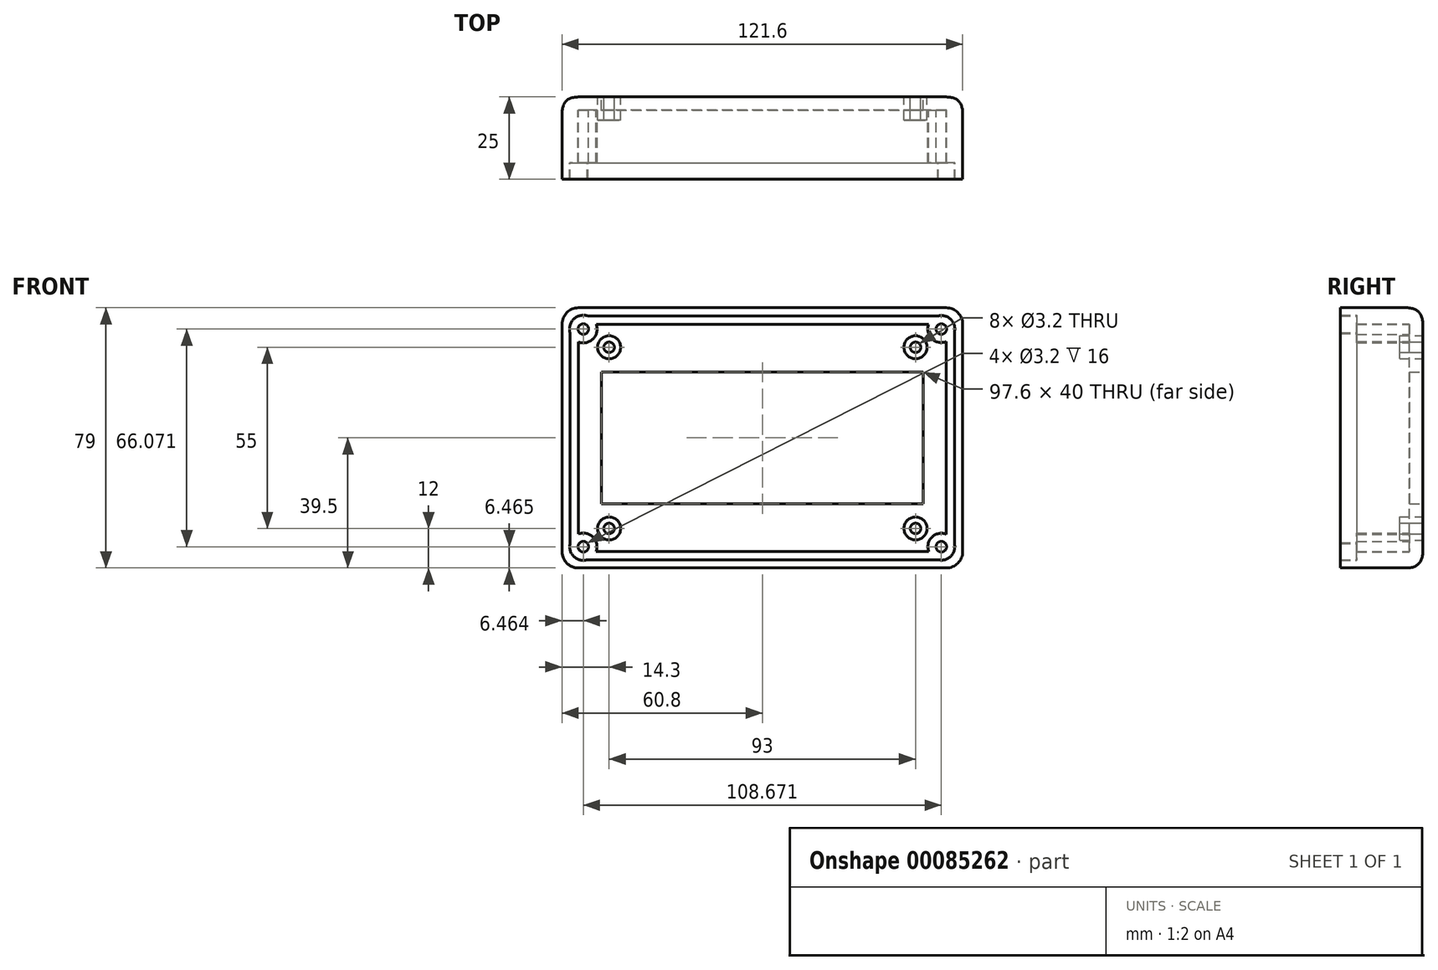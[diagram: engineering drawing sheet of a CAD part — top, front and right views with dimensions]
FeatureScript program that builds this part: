
annotation { "Feature Type Name" : "Feature", "Feature Type Description" : "" }
export const myFeature = defineFeature(function(context is Context, id is Id, definition is map)
    precondition{}
    {
        {
            var Q0;
            Q0=qCreatedBy(makeId("Front.planeOp"),FACE);
            var sketch = newSketch(context, id + "F0", { "sketchPlane" : qUnion([Q0])});
            skLineSegment(sketch, "E0.bottom", {"start": v(55.8, 39.5) * mm, "end": v(-55.8, 39.5) * mm});
            skLineSegment(sketch, "E0.top", {"start": v(55.8, -39.5) * mm, "end": v(-55.8, -39.5) * mm});
            skLineSegment(sketch, "E0.left", {"start": v(60.8, 34.5) * mm, "end": v(60.8, -34.5) * mm});
            skLineSegment(sketch, "E0.right", {"start": v(-60.8, 34.5) * mm, "end": v(-60.8, -34.5) * mm});
            skPoint(sketch, "E0.middle", {"position": v(0, 0) * mm});
            skPoint(sketch, "E1.visualSharp", {"position": v(-60.8, 39.5) * mm});
            skArc(sketch, "E1.filletArc", {"start": v(-55.8, 39.5) * mm, "mid": v(-59.34, 38.04) * mm, "end": v(-60.8, 34.5) * mm});
            skPoint(sketch, "E2.visualSharp", {"position": v(60.8, 39.5) * mm});
            skArc(sketch, "E2.filletArc", {"start": v(60.8, 34.5) * mm, "mid": v(59.34, 38.04) * mm, "end": v(55.8, 39.5) * mm});
            skPoint(sketch, "E3.visualSharp", {"position": v(60.8, -39.5) * mm});
            skArc(sketch, "E3.filletArc", {"start": v(55.8, -39.5) * mm, "mid": v(59.34, -38.04) * mm, "end": v(60.8, -34.5) * mm});
            skPoint(sketch, "E4.visualSharp", {"position": v(-60.8, -39.5) * mm});
            skArc(sketch, "E4.filletArc", {"start": v(-60.8, -34.5) * mm, "mid": v(-59.34, -38.04) * mm, "end": v(-55.8, -39.5) * mm});
            skLineSegment(sketch, "E5.bottom", {"start": v(-46.5, 27.5) * mm, "end": v(46.5, 27.5) * mm});
            skLineSegment(sketch, "E5.top", {"start": v(-46.5, -27.5) * mm, "end": v(46.5, -27.5) * mm});
            skLineSegment(sketch, "E5.left", {"start": v(-46.5, 27.5) * mm, "end": v(-46.5, -27.5) * mm});
            skLineSegment(sketch, "E5.right", {"start": v(46.5, 27.5) * mm, "end": v(46.5, -27.5) * mm});
            skCircle(sketch, "E6", {"center": v(-46.5, 27.5) * mm, "radius": 1.6 * mm});
            skCircle(sketch, "E7", {"center": v(-46.5, 27.5) * mm, "radius": 3.5 * mm});
            skCircle(sketch, "E8", {"center": v(46.5, 27.5) * mm, "radius": 1.6 * mm});
            skCircle(sketch, "E9", {"center": v(46.5, 27.5) * mm, "radius": 3.5 * mm});
            skCircle(sketch, "E10", {"center": v(46.5, -27.5) * mm, "radius": 1.6 * mm});
            skCircle(sketch, "E11", {"center": v(46.5, -27.5) * mm, "radius": 3.5 * mm});
            skCircle(sketch, "E12", {"center": v(-46.5, -27.5) * mm, "radius": 1.6 * mm});
            skCircle(sketch, "E13", {"center": v(-46.5, -27.5) * mm, "radius": 3.5 * mm});
            skLineSegment(sketch, "E14.bottom", {"start": v(-48.8, 20) * mm, "end": v(48.8, 20) * mm});
            skLineSegment(sketch, "E14.top", {"start": v(-48.8, -20) * mm, "end": v(48.8, -20) * mm});
            skLineSegment(sketch, "E14.left", {"start": v(-48.8, 20) * mm, "end": v(-48.8, -20) * mm});
            skLineSegment(sketch, "E14.right", {"start": v(48.8, 20) * mm, "end": v(48.8, -20) * mm});
            skLineSegment(sketch, "E15.bottom", {"start": v(-50.8, 34.5) * mm, "end": v(50.8, 34.5) * mm});
            skLineSegment(sketch, "E15.top", {"start": v(-50.8, -34.5) * mm, "end": v(50.8, -34.5) * mm});
            skLineSegment(sketch, "E15.left", {"start": v(-55.8, 29.5) * mm, "end": v(-55.8, -29.5) * mm});
            skLineSegment(sketch, "E15.right", {"start": v(55.8, 29.5) * mm, "end": v(55.8, -29.5) * mm});
            skArc(sketch, "E16.filletArc", {"start": v(-50.8, 34.5) * mm, "mid": v(-54.34, 33.04) * mm, "end": v(-55.8, 29.5) * mm});
            skArc(sketch, "E17.filletArc", {"start": v(55.8, 29.5) * mm, "mid": v(54.34, 33.04) * mm, "end": v(50.8, 34.5) * mm});
            skArc(sketch, "E18.filletArc", {"start": v(50.8, -34.5) * mm, "mid": v(54.34, -33.04) * mm, "end": v(55.8, -29.5) * mm});
            skArc(sketch, "E19.filletArc", {"start": v(-55.8, -29.5) * mm, "mid": v(-54.34, -33.04) * mm, "end": v(-50.8, -34.5) * mm});
            skLineSegment(sketch, "E20.bottom", {"start": v(-53.3, 37) * mm, "end": v(53.3, 37) * mm});
            skLineSegment(sketch, "E20.top", {"start": v(-53.3, -37) * mm, "end": v(53.3, -37) * mm});
            skLineSegment(sketch, "E20.left", {"start": v(-58.3, 32) * mm, "end": v(-58.3, -32) * mm});
            skLineSegment(sketch, "E20.right", {"start": v(58.3, 32) * mm, "end": v(58.3, -32) * mm});
            skPoint(sketch, "E21.visualSharp", {"position": v(-58.3, 37) * mm});
            skArc(sketch, "E21.filletArc", {"start": v(-53.3, 37) * mm, "mid": v(-56.84, 35.54) * mm, "end": v(-58.3, 32) * mm});
            skPoint(sketch, "E22.visualSharp", {"position": v(58.3, 37) * mm});
            skArc(sketch, "E22.filletArc", {"start": v(58.3, 32) * mm, "mid": v(56.84, 35.54) * mm, "end": v(53.3, 37) * mm});
            skPoint(sketch, "E23.visualSharp", {"position": v(58.3, -37) * mm});
            skArc(sketch, "E23.filletArc", {"start": v(53.3, -37) * mm, "mid": v(56.84, -35.54) * mm, "end": v(58.3, -32) * mm});
            skPoint(sketch, "E24.visualSharp", {"position": v(-58.3, -37) * mm});
            skArc(sketch, "E24.filletArc", {"start": v(-58.3, -32) * mm, "mid": v(-56.84, -35.54) * mm, "end": v(-53.3, -37) * mm});
            skCircle(sketch, "E25", {"center": v(-54.34, 33.04) * mm, "radius": 4.2 * mm});
            skCircle(sketch, "E26", {"center": v(-54.34, 33.04) * mm, "radius": 1.6 * mm});
            skCircle(sketch, "E27", {"center": v(54.34, 33.04) * mm, "radius": 1.6 * mm});
            skCircle(sketch, "E28", {"center": v(54.34, 33.04) * mm, "radius": 4.1 * mm});
            skCircle(sketch, "E29", {"center": v(54.34, -33.04) * mm, "radius": 1.6 * mm});
            skCircle(sketch, "E30", {"center": v(54.34, -33.04) * mm, "radius": 4.09 * mm});
            skCircle(sketch, "E31", {"center": v(-54.34, -33.04) * mm, "radius": 1.6 * mm});
            skCircle(sketch, "E32", {"center": v(-54.34, -33.04) * mm, "radius": 4.14 * mm});
            skSolve(sketch);
        }
        {
            var Q0;
            {var subQ0=sQuery(id+"F0.wireOp",EDGE,"E6");var subQ1=sQuery(id+"F0.wireOp",EDGE,"E5.bottom");var subQ2=makeQuery(id+"F0.imprint","INTERSECT",VERTEX,{"derivedFrom":[subQ1,subQ0]});Q0=makeQuery(id+"F0.imprint","IMPRINT",FACE,{"disambiguationData":[TD([[makeQuery(id+"F0.imprint","IMPRINT",EDGE,{"disambiguationData":[TD([[subQ2,-1.0]])],"derivedFrom":subQ1}),1.0]])]});}
            var Q1;
            {var subQ0=sQuery(id+"F0.wireOp",EDGE,"E6");var subQ1=sQuery(id+"F0.wireOp",EDGE,"E5.bottom");var subQ2=makeQuery(id+"F0.imprint","INTERSECT",VERTEX,{"derivedFrom":[subQ1,subQ0]});Q1=makeQuery(id+"F0.imprint","IMPRINT",FACE,{"disambiguationData":[TD([[makeQuery(id+"F0.imprint","IMPRINT",EDGE,{"disambiguationData":[TD([[subQ2,-1.0]])],"derivedFrom":subQ1}),-1.0]])]});}
            var Q2;
            {var subQ3=sQuery(id+"F0.wireOp",EDGE,"E12");var subQ9=sQuery(id+"F0.wireOp",EDGE,"E5.top");var subQ12=makeQuery(id+"F0.imprint","INTERSECT",VERTEX,{"derivedFrom":[subQ9,subQ3]});Q2=makeQuery(id+"F0.imprint","IMPRINT",FACE,{"disambiguationData":[TD([[makeQuery(id+"F0.imprint","IMPRINT",EDGE,{"disambiguationData":[TD([[subQ12,-1.0]])],"derivedFrom":subQ9}),1.0]])]});}
            var Q3;
            {var subQ0=sQuery(id+"F0.wireOp",EDGE,"E12");var subQ1=sQuery(id+"F0.wireOp",EDGE,"E5.top");var subQ2=makeQuery(id+"F0.imprint","INTERSECT",VERTEX,{"derivedFrom":[subQ1,subQ0]});Q3=makeQuery(id+"F0.imprint","IMPRINT",FACE,{"disambiguationData":[TD([[makeQuery(id+"F0.imprint","IMPRINT",EDGE,{"disambiguationData":[TD([[subQ2,-1.0]])],"derivedFrom":subQ1}),-1.0]])]});}
            var Q4;
            {var subQ0=sQuery(id+"F0.wireOp",EDGE,"E11");var subQ1=sQuery(id+"F0.wireOp",EDGE,"E5.top");var subQ2=makeQuery(id+"F0.imprint","INTERSECT",VERTEX,{"derivedFrom":[subQ1,subQ0]});Q4=makeQuery(id+"F0.imprint","IMPRINT",FACE,{"disambiguationData":[TD([[makeQuery(id+"F0.imprint","IMPRINT",EDGE,{"disambiguationData":[TD([[subQ2,-1.0]])],"derivedFrom":subQ1}),-1.0]])]});}
            var Q5;
            {var subQ1=sQuery(id+"F0.wireOp",EDGE,"E5.top");var subQ5=sQuery(id+"F0.wireOp",EDGE,"E11");var subQ6=makeQuery(id+"F0.imprint","INTERSECT",VERTEX,{"derivedFrom":[subQ1,subQ5]});Q5=makeQuery(id+"F0.imprint","IMPRINT",FACE,{"disambiguationData":[TD([[makeQuery(id+"F0.imprint","IMPRINT",EDGE,{"disambiguationData":[TD([[subQ6,-1.0]])],"derivedFrom":subQ1}),1.0]])]});}
            var Q6;
            {var subQ0=sQuery(id+"F0.wireOp",EDGE,"E13");var subQ1=sQuery(id+"F0.wireOp",EDGE,"E5.top");var subQ2=makeQuery(id+"F0.imprint","INTERSECT",VERTEX,{"derivedFrom":[subQ1,subQ0]});Q6=makeQuery(id+"F0.imprint","IMPRINT",FACE,{"disambiguationData":[TD([[makeQuery(id+"F0.imprint","IMPRINT",EDGE,{"disambiguationData":[TD([[subQ2,-1.0]])],"derivedFrom":subQ1}),1.0]])]});}
            var Q7;
            {var subQ0=sQuery(id+"F0.wireOp",EDGE,"E9");var subQ1=sQuery(id+"F0.wireOp",EDGE,"E5.bottom");var subQ2=makeQuery(id+"F0.imprint","INTERSECT",VERTEX,{"derivedFrom":[subQ1,subQ0]});Q7=makeQuery(id+"F0.imprint","IMPRINT",FACE,{"disambiguationData":[TD([[makeQuery(id+"F0.imprint","IMPRINT",EDGE,{"disambiguationData":[TD([[subQ2,-1.0]])],"derivedFrom":subQ1}),1.0]])]});}
            var Q8;
            {var subQ0=sQuery(id+"F0.wireOp",EDGE,"E9");var subQ1=sQuery(id+"F0.wireOp",EDGE,"E5.bottom");var subQ2=makeQuery(id+"F0.imprint","INTERSECT",VERTEX,{"derivedFrom":[subQ1,subQ0]});Q8=makeQuery(id+"F0.imprint","IMPRINT",FACE,{"disambiguationData":[TD([[makeQuery(id+"F0.imprint","IMPRINT",EDGE,{"disambiguationData":[TD([[subQ2,-1.0]])],"derivedFrom":subQ1}),-1.0]])]});}
            var Q9;
            {var subQ5=sQuery(id+"F0.wireOp",EDGE,"E7");var subQ9=sQuery(id+"F0.wireOp",EDGE,"E5.bottom");var subQ10=makeQuery(id+"F0.imprint","INTERSECT",VERTEX,{"derivedFrom":[subQ9,subQ5]});Q9=makeQuery(id+"F0.imprint","IMPRINT",FACE,{"disambiguationData":[TD([[makeQuery(id+"F0.imprint","IMPRINT",EDGE,{"disambiguationData":[TD([[subQ10,-1.0]])],"derivedFrom":subQ9}),-1.0]])]});}
            var Q10;
            {var subQ12=sQuery(id+"F0.wireOp",EDGE,"E14.left");Q10=makeQuery(id+"F0.imprint","IMPRINT",FACE,{"disambiguationData":[TD([[makeQuery(id+"F0.imprint","IMPRINT",EDGE,{"derivedFrom":subQ12}),-1.0]])]});}
            var Q11;
            {var subQ4=sQuery(id+"F0.wireOp",EDGE,"E15.bottom");Q11=makeQuery(id+"F0.imprint","IMPRINT",FACE,{"disambiguationData":[TD([[makeQuery(id+"F0.imprint","IMPRINT",EDGE,{"derivedFrom":subQ4}),1.0]])]});}
            var Q12;
            Q12=makeQuery(id+"F0.imprint","IMPRINT",FACE,{"disambiguationData":[TD([[makeQuery(id+"F0.imprint","IMPRINT",EDGE,{"derivedFrom":sQuery(id+"F0.wireOp",EDGE,"E15.top")}),-1.0]])]});
            var Q13;
            {var subQ0=sQuery(id+"F0.wireOp",EDGE,"E16.filletArc");var subQ5=sQuery(id+"F0.wireOp",EDGE,"E15.bottom");var subQ6=makeQuery(id+"F0.imprint","INTERSECT",VERTEX,{"derivedFrom":[subQ5,subQ0]});Q13=makeQuery(id+"F0.imprint","IMPRINT",FACE,{"disambiguationData":[TD([[makeQuery(id+"F0.imprint","IMPRINT",EDGE,{"disambiguationData":[TD([[subQ6,-1.0]])],"derivedFrom":subQ5}),-1.0]])]});}
            var Q14;
            {var subQ0=sQuery(id+"F0.wireOp",EDGE,"E21.filletArc");Q14=makeQuery(id+"F0.imprint","IMPRINT",FACE,{"disambiguationData":[TD([[makeQuery(id+"F0.imprint","IMPRINT",EDGE,{"derivedFrom":subQ0}),-1.0]])]});}
            var Q15;
            {var subQ0=sQuery(id+"F0.wireOp",EDGE,"E24.filletArc");Q15=makeQuery(id+"F0.imprint","IMPRINT",FACE,{"disambiguationData":[TD([[makeQuery(id+"F0.imprint","IMPRINT",EDGE,{"derivedFrom":subQ0}),-1.0]])]});}
            var Q16;
            {var subQ11=sQuery(id+"F0.wireOp",EDGE,"E24.filletArc");Q16=makeQuery(id+"F0.imprint","IMPRINT",FACE,{"disambiguationData":[TD([[makeQuery(id+"F0.imprint","IMPRINT",EDGE,{"derivedFrom":subQ11}),1.0]])]});}
            var Q17;
            {var subQ0=sQuery(id+"F0.wireOp",EDGE,"E19.filletArc");var subQ1=sQuery(id+"F0.wireOp",EDGE,"E15.top");var subQ2=makeQuery(id+"F0.imprint","INTERSECT",VERTEX,{"derivedFrom":[subQ1,subQ0]});Q17=makeQuery(id+"F0.imprint","IMPRINT",FACE,{"disambiguationData":[TD([[makeQuery(id+"F0.imprint","IMPRINT",EDGE,{"disambiguationData":[TD([[subQ2,-1.0]])],"derivedFrom":subQ1}),1.0]])]});}
            var Q18;
            {var subQ0=sQuery(id+"F0.wireOp",EDGE,"E25");var subQ1=sQuery(id+"F0.wireOp",EDGE,"E15.left");var subQ2=makeQuery(id+"F0.imprint","INTERSECT",VERTEX,{"derivedFrom":[subQ1,subQ0]});Q18=makeQuery(id+"F0.imprint","IMPRINT",FACE,{"disambiguationData":[TD([[makeQuery(id+"F0.imprint","IMPRINT",EDGE,{"disambiguationData":[TD([[subQ2,-1.0]])],"derivedFrom":subQ1}),-1.0]])]});}
            var Q19;
            {var subQ11=sQuery(id+"F0.wireOp",EDGE,"E21.filletArc");Q19=makeQuery(id+"F0.imprint","IMPRINT",FACE,{"disambiguationData":[TD([[makeQuery(id+"F0.imprint","IMPRINT",EDGE,{"derivedFrom":subQ11}),1.0]])]});}
            var Q20;
            {var subQ0=sQuery(id+"F0.wireOp",EDGE,"E18.filletArc");var subQ1=sQuery(id+"F0.wireOp",EDGE,"E15.top");var subQ2=makeQuery(id+"F0.imprint","INTERSECT",VERTEX,{"derivedFrom":[subQ1,subQ0]});Q20=makeQuery(id+"F0.imprint","IMPRINT",FACE,{"disambiguationData":[TD([[makeQuery(id+"F0.imprint","IMPRINT",EDGE,{"disambiguationData":[TD([[subQ2,1.0]])],"derivedFrom":subQ1}),1.0]])]});}
            var Q21;
            {var subQ0=sQuery(id+"F0.wireOp",EDGE,"E18.filletArc");var subQ1=sQuery(id+"F0.wireOp",EDGE,"E15.top");var subQ2=makeQuery(id+"F0.imprint","INTERSECT",VERTEX,{"derivedFrom":[subQ1,subQ0]});Q21=makeQuery(id+"F0.imprint","IMPRINT",FACE,{"disambiguationData":[TD([[makeQuery(id+"F0.imprint","IMPRINT",EDGE,{"disambiguationData":[TD([[subQ2,1.0]])],"derivedFrom":subQ1}),-1.0]])]});}
            var Q22;
            Q22=makeQuery(id+"F0.imprint","IMPRINT",FACE,{"disambiguationData":[TD([[makeQuery(id+"F0.imprint","IMPRINT",EDGE,{"derivedFrom":sQuery(id+"F0.wireOp",EDGE,"E0.bottom")}),1.0]])]});
            var Q23;
            {var subQ0=sQuery(id+"F0.wireOp",EDGE,"E30");var subQ1=sQuery(id+"F0.wireOp",EDGE,"E23.filletArc");var subQ2=makeQuery(id+"F0.imprint","INTERSECT",VERTEX,{"disambiguationData":[OD(0.0)],"derivedFrom":[subQ1,subQ0]});Q23=makeQuery(id+"F0.imprint","IMPRINT",FACE,{"disambiguationData":[TD([[makeQuery(id+"F0.imprint","IMPRINT",EDGE,{"disambiguationData":[TD([[subQ2,-1.0]])],"derivedFrom":subQ1}),-1.0]])]});}
            var Q24;
            {var subQ0=sQuery(id+"F0.wireOp",EDGE,"E28");var subQ1=sQuery(id+"F0.wireOp",EDGE,"E15.right");var subQ2=makeQuery(id+"F0.imprint","INTERSECT",VERTEX,{"derivedFrom":[subQ1,subQ0]});Q24=makeQuery(id+"F0.imprint","IMPRINT",FACE,{"disambiguationData":[TD([[makeQuery(id+"F0.imprint","IMPRINT",EDGE,{"disambiguationData":[TD([[subQ2,-1.0]])],"derivedFrom":subQ1}),1.0]])]});}
            var Q25;
            {var subQ0=sQuery(id+"F0.wireOp",EDGE,"E22.filletArc");Q25=makeQuery(id+"F0.imprint","IMPRINT",FACE,{"disambiguationData":[TD([[makeQuery(id+"F0.imprint","IMPRINT",EDGE,{"derivedFrom":subQ0}),-1.0]])]});}
            var Q26;
            {var subQ10=sQuery(id+"F0.wireOp",EDGE,"E22.filletArc");Q26=makeQuery(id+"F0.imprint","IMPRINT",FACE,{"disambiguationData":[TD([[makeQuery(id+"F0.imprint","IMPRINT",EDGE,{"derivedFrom":subQ10}),1.0]])]});}
            var Q27;
            {var subQ0=sQuery(id+"F0.wireOp",EDGE,"E17.filletArc");var subQ7=sQuery(id+"F0.wireOp",EDGE,"E15.bottom");var subQ8=makeQuery(id+"F0.imprint","INTERSECT",VERTEX,{"derivedFrom":[subQ7,subQ0]});Q27=makeQuery(id+"F0.imprint","IMPRINT",FACE,{"disambiguationData":[TD([[makeQuery(id+"F0.imprint","IMPRINT",EDGE,{"disambiguationData":[TD([[subQ8,1.0]])],"derivedFrom":subQ7}),-1.0]])]});}
            var Q28;
            {var subQ0=sQuery(id+"F0.wireOp",EDGE,"E26");var subQ1=sQuery(id+"F0.wireOp",EDGE,"E16.filletArc");var subQ2=makeQuery(id+"F0.imprint","INTERSECT",VERTEX,{"disambiguationData":[OD(0.0)],"derivedFrom":[subQ1,subQ0]});Q28=makeQuery(id+"F0.imprint","IMPRINT",FACE,{"disambiguationData":[TD([[makeQuery(id+"F0.imprint","IMPRINT",EDGE,{"disambiguationData":[TD([[subQ2,-1.0]])],"derivedFrom":subQ1}),-1.0]])]});}
            var Q29;
            {var subQ0=sQuery(id+"F0.wireOp",EDGE,"E26");var subQ1=sQuery(id+"F0.wireOp",EDGE,"E16.filletArc");var subQ2=makeQuery(id+"F0.imprint","INTERSECT",VERTEX,{"disambiguationData":[OD(0.0)],"derivedFrom":[subQ1,subQ0]});Q29=makeQuery(id+"F0.imprint","IMPRINT",FACE,{"disambiguationData":[TD([[makeQuery(id+"F0.imprint","IMPRINT",EDGE,{"disambiguationData":[TD([[subQ2,-1.0]])],"derivedFrom":subQ1}),1.0]])]});}
            var Q30;
            {var subQ0=sQuery(id+"F0.wireOp",EDGE,"E27");var subQ1=sQuery(id+"F0.wireOp",EDGE,"E17.filletArc");var subQ2=makeQuery(id+"F0.imprint","INTERSECT",VERTEX,{"disambiguationData":[OD(0.0)],"derivedFrom":[subQ1,subQ0]});Q30=makeQuery(id+"F0.imprint","IMPRINT",FACE,{"disambiguationData":[TD([[makeQuery(id+"F0.imprint","IMPRINT",EDGE,{"disambiguationData":[TD([[subQ2,-1.0]])],"derivedFrom":subQ1}),-1.0]])]});}
            var Q31;
            {var subQ0=sQuery(id+"F0.wireOp",EDGE,"E27");var subQ1=sQuery(id+"F0.wireOp",EDGE,"E17.filletArc");var subQ2=makeQuery(id+"F0.imprint","INTERSECT",VERTEX,{"disambiguationData":[OD(0.0)],"derivedFrom":[subQ1,subQ0]});Q31=makeQuery(id+"F0.imprint","IMPRINT",FACE,{"disambiguationData":[TD([[makeQuery(id+"F0.imprint","IMPRINT",EDGE,{"disambiguationData":[TD([[subQ2,-1.0]])],"derivedFrom":subQ1}),1.0]])]});}
            var Q32;
            {var subQ0=sQuery(id+"F0.wireOp",EDGE,"E29");var subQ1=sQuery(id+"F0.wireOp",EDGE,"E18.filletArc");var subQ2=makeQuery(id+"F0.imprint","INTERSECT",VERTEX,{"disambiguationData":[OD(0.0)],"derivedFrom":[subQ1,subQ0]});Q32=makeQuery(id+"F0.imprint","IMPRINT",FACE,{"disambiguationData":[TD([[makeQuery(id+"F0.imprint","IMPRINT",EDGE,{"disambiguationData":[TD([[subQ2,-1.0]])],"derivedFrom":subQ1}),-1.0]])]});}
            var Q33;
            {var subQ0=sQuery(id+"F0.wireOp",EDGE,"E29");var subQ1=sQuery(id+"F0.wireOp",EDGE,"E18.filletArc");var subQ2=makeQuery(id+"F0.imprint","INTERSECT",VERTEX,{"disambiguationData":[OD(0.0)],"derivedFrom":[subQ1,subQ0]});Q33=makeQuery(id+"F0.imprint","IMPRINT",FACE,{"disambiguationData":[TD([[makeQuery(id+"F0.imprint","IMPRINT",EDGE,{"disambiguationData":[TD([[subQ2,-1.0]])],"derivedFrom":subQ1}),1.0]])]});}
            var Q34;
            {var subQ0=sQuery(id+"F0.wireOp",EDGE,"E31");var subQ1=sQuery(id+"F0.wireOp",EDGE,"E19.filletArc");var subQ2=makeQuery(id+"F0.imprint","INTERSECT",VERTEX,{"disambiguationData":[OD(0.0)],"derivedFrom":[subQ1,subQ0]});Q34=makeQuery(id+"F0.imprint","IMPRINT",FACE,{"disambiguationData":[TD([[makeQuery(id+"F0.imprint","IMPRINT",EDGE,{"disambiguationData":[TD([[subQ2,-1.0]])],"derivedFrom":subQ1}),1.0]])]});}
            var Q35;
            {var subQ0=sQuery(id+"F0.wireOp",EDGE,"E31");var subQ1=sQuery(id+"F0.wireOp",EDGE,"E19.filletArc");var subQ2=makeQuery(id+"F0.imprint","INTERSECT",VERTEX,{"disambiguationData":[OD(0.0)],"derivedFrom":[subQ1,subQ0]});Q35=makeQuery(id+"F0.imprint","IMPRINT",FACE,{"disambiguationData":[TD([[makeQuery(id+"F0.imprint","IMPRINT",EDGE,{"disambiguationData":[TD([[subQ2,-1.0]])],"derivedFrom":subQ1}),-1.0]])]});}
            extrude(context, id + "F1", {"entities" : qUnion([Q0, Q1, Q2, Q3, Q4, Q5, Q6, Q7, Q8, Q9, Q10, Q11, Q12, Q13, Q14, Q15, Q16, Q17, Q18, Q19, Q20, Q21, Q22, Q23, Q24, Q25, Q26, Q27, Q28, Q29, Q30, Q31, Q32, Q33, Q34, Q35]), "depth" : 4 * mm});
        }
        {
            var Q0;
            {var subQ0=sQuery(id+"F0.wireOp",EDGE,"E12");var subQ1=sQuery(id+"F0.wireOp",EDGE,"E5.top");var subQ2=makeQuery(id+"F0.imprint","INTERSECT",VERTEX,{"derivedFrom":[subQ1,subQ0]});Q0=makeQuery(id+"F0.imprint","IMPRINT",FACE,{"disambiguationData":[TD([[makeQuery(id+"F0.imprint","IMPRINT",EDGE,{"disambiguationData":[TD([[subQ2,-1.0]])],"derivedFrom":subQ1}),-1.0]])]});}
            var Q1;
            {var subQ3=sQuery(id+"F0.wireOp",EDGE,"E12");var subQ9=sQuery(id+"F0.wireOp",EDGE,"E5.top");var subQ12=makeQuery(id+"F0.imprint","INTERSECT",VERTEX,{"derivedFrom":[subQ9,subQ3]});Q1=makeQuery(id+"F0.imprint","IMPRINT",FACE,{"disambiguationData":[TD([[makeQuery(id+"F0.imprint","IMPRINT",EDGE,{"disambiguationData":[TD([[subQ12,-1.0]])],"derivedFrom":subQ9}),1.0]])]});}
            var Q2;
            {var subQ0=sQuery(id+"F0.wireOp",EDGE,"E11");var subQ1=sQuery(id+"F0.wireOp",EDGE,"E5.top");var subQ2=makeQuery(id+"F0.imprint","INTERSECT",VERTEX,{"derivedFrom":[subQ1,subQ0]});Q2=makeQuery(id+"F0.imprint","IMPRINT",FACE,{"disambiguationData":[TD([[makeQuery(id+"F0.imprint","IMPRINT",EDGE,{"disambiguationData":[TD([[subQ2,-1.0]])],"derivedFrom":subQ1}),-1.0]])]});}
            var Q3;
            {var subQ1=sQuery(id+"F0.wireOp",EDGE,"E5.top");var subQ5=sQuery(id+"F0.wireOp",EDGE,"E11");var subQ6=makeQuery(id+"F0.imprint","INTERSECT",VERTEX,{"derivedFrom":[subQ1,subQ5]});Q3=makeQuery(id+"F0.imprint","IMPRINT",FACE,{"disambiguationData":[TD([[makeQuery(id+"F0.imprint","IMPRINT",EDGE,{"disambiguationData":[TD([[subQ6,-1.0]])],"derivedFrom":subQ1}),1.0]])]});}
            var Q4;
            {var subQ0=sQuery(id+"F0.wireOp",EDGE,"E9");var subQ1=sQuery(id+"F0.wireOp",EDGE,"E5.bottom");var subQ2=makeQuery(id+"F0.imprint","INTERSECT",VERTEX,{"derivedFrom":[subQ1,subQ0]});Q4=makeQuery(id+"F0.imprint","IMPRINT",FACE,{"disambiguationData":[TD([[makeQuery(id+"F0.imprint","IMPRINT",EDGE,{"disambiguationData":[TD([[subQ2,-1.0]])],"derivedFrom":subQ1}),1.0]])]});}
            var Q5;
            {var subQ0=sQuery(id+"F0.wireOp",EDGE,"E9");var subQ1=sQuery(id+"F0.wireOp",EDGE,"E5.bottom");var subQ2=makeQuery(id+"F0.imprint","INTERSECT",VERTEX,{"derivedFrom":[subQ1,subQ0]});Q5=makeQuery(id+"F0.imprint","IMPRINT",FACE,{"disambiguationData":[TD([[makeQuery(id+"F0.imprint","IMPRINT",EDGE,{"disambiguationData":[TD([[subQ2,-1.0]])],"derivedFrom":subQ1}),-1.0]])]});}
            var Q6;
            {var subQ0=sQuery(id+"F0.wireOp",EDGE,"E6");var subQ1=sQuery(id+"F0.wireOp",EDGE,"E5.bottom");var subQ2=makeQuery(id+"F0.imprint","INTERSECT",VERTEX,{"derivedFrom":[subQ1,subQ0]});Q6=makeQuery(id+"F0.imprint","IMPRINT",FACE,{"disambiguationData":[TD([[makeQuery(id+"F0.imprint","IMPRINT",EDGE,{"disambiguationData":[TD([[subQ2,-1.0]])],"derivedFrom":subQ1}),1.0]])]});}
            var Q7;
            {var subQ0=sQuery(id+"F0.wireOp",EDGE,"E6");var subQ1=sQuery(id+"F0.wireOp",EDGE,"E5.bottom");var subQ2=makeQuery(id+"F0.imprint","INTERSECT",VERTEX,{"derivedFrom":[subQ1,subQ0]});Q7=makeQuery(id+"F0.imprint","IMPRINT",FACE,{"disambiguationData":[TD([[makeQuery(id+"F0.imprint","IMPRINT",EDGE,{"disambiguationData":[TD([[subQ2,-1.0]])],"derivedFrom":subQ1}),-1.0]])]});}
            extrude(context, id + "F2", {"entities" : qUnion([Q0, Q1, Q2, Q3, Q4, Q5, Q6, Q7]), "depth" : 7 * mm});
        }
        {
            var Q0;
            Q0=makeQuery(id+"F0.imprint","IMPRINT",FACE,{"disambiguationData":[TD([[makeQuery(id+"F0.imprint","IMPRINT",EDGE,{"derivedFrom":sQuery(id+"F0.wireOp",EDGE,"E0.bottom")}),1.0]])]});
            extrude(context, id + "F3", {"entities" : qUnion([Q0]), "operationType" : NewBodyOperationType.ADD, "depth" : 25 * mm});
        }
        {
            var Q0;
            Q0=makeQuery(id+"F1.opExtrude","CAP_EDGE",EDGE,{"disambiguationData":[OSD([sQuery(id+"F0.wireOp",EDGE,"E2.filletArc")])],"isStart":true});
            var Q1;
            Q1=makeQuery(id+"F1.opExtrude","CAP_EDGE",EDGE,{"disambiguationData":[OSD([sQuery(id+"F0.wireOp",EDGE,"E0.left")])],"isStart":true});
            var Q2;
            Q2=makeQuery(id+"F1.opExtrude","CAP_EDGE",EDGE,{"disambiguationData":[OSD([sQuery(id+"F0.wireOp",EDGE,"E3.filletArc")])],"isStart":true});
            var Q3;
            Q3=makeQuery(id+"F1.opExtrude","CAP_EDGE",EDGE,{"disambiguationData":[OSD([sQuery(id+"F0.wireOp",EDGE,"E0.top")])],"isStart":true});
            var Q4;
            Q4=makeQuery(id+"F1.opExtrude","CAP_EDGE",EDGE,{"disambiguationData":[OSD([sQuery(id+"F0.wireOp",EDGE,"E4.filletArc")])],"isStart":true});
            var Q5;
            Q5=makeQuery(id+"F1.opExtrude","CAP_EDGE",EDGE,{"disambiguationData":[OSD([sQuery(id+"F0.wireOp",EDGE,"E0.right")])],"isStart":true});
            var Q6;
            Q6=makeQuery(id+"F1.opExtrude","CAP_EDGE",EDGE,{"disambiguationData":[OSD([sQuery(id+"F0.wireOp",EDGE,"E1.filletArc")])],"isStart":true});
            var Q7;
            Q7=makeQuery(id+"F1.opExtrude","CAP_EDGE",EDGE,{"disambiguationData":[OSD([sQuery(id+"F0.wireOp",EDGE,"E0.bottom")])],"isStart":true});
            fillet(context, id + "F4", {"entities" : qUnion([Q0, Q1, Q2, Q3, Q4, Q5, Q6, Q7]), "radius" : 5 * mm, "tangentPropagation" : true, "rho" : 0.5, "crossSection" : FilletCrossSection.CONIC, "allowEdgeOverflow" : false});
        }
        {
            var Q0;
            {var subQ0=sQuery(id+"F0.wireOp",EDGE,"E25");var subQ1=sQuery(id+"F0.wireOp",EDGE,"E15.bottom");var subQ2=makeQuery(id+"F0.imprint","INTERSECT",VERTEX,{"derivedFrom":[subQ1,subQ0]});Q0=makeQuery(id+"F0.imprint","IMPRINT",FACE,{"disambiguationData":[TD([[makeQuery(id+"F0.imprint","IMPRINT",EDGE,{"disambiguationData":[TD([[subQ2,-1.0]])],"derivedFrom":subQ1}),1.0]])]});}
            var Q1;
            {var subQ11=sQuery(id+"F0.wireOp",EDGE,"E21.filletArc");Q1=makeQuery(id+"F0.imprint","IMPRINT",FACE,{"disambiguationData":[TD([[makeQuery(id+"F0.imprint","IMPRINT",EDGE,{"derivedFrom":subQ11}),1.0]])]});}
            var Q2;
            {var subQ0=sQuery(id+"F0.wireOp",EDGE,"E16.filletArc");var subQ5=sQuery(id+"F0.wireOp",EDGE,"E15.bottom");var subQ6=makeQuery(id+"F0.imprint","INTERSECT",VERTEX,{"derivedFrom":[subQ5,subQ0]});Q2=makeQuery(id+"F0.imprint","IMPRINT",FACE,{"disambiguationData":[TD([[makeQuery(id+"F0.imprint","IMPRINT",EDGE,{"disambiguationData":[TD([[subQ6,-1.0]])],"derivedFrom":subQ5}),-1.0]])]});}
            var Q3;
            {var subQ0=sQuery(id+"F0.wireOp",EDGE,"E25");var subQ1=sQuery(id+"F0.wireOp",EDGE,"E15.left");var subQ2=makeQuery(id+"F0.imprint","INTERSECT",VERTEX,{"derivedFrom":[subQ1,subQ0]});Q3=makeQuery(id+"F0.imprint","IMPRINT",FACE,{"disambiguationData":[TD([[makeQuery(id+"F0.imprint","IMPRINT",EDGE,{"disambiguationData":[TD([[subQ2,-1.0]])],"derivedFrom":subQ1}),-1.0]])]});}
            var Q4;
            Q4=makeQuery(id+"F0.imprint","IMPRINT",FACE,{"disambiguationData":[TD([[makeQuery(id+"F0.imprint","IMPRINT",EDGE,{"derivedFrom":sQuery(id+"F0.wireOp",EDGE,"E0.bottom")}),1.0]])]});
            var Q5;
            {var subQ11=sQuery(id+"F0.wireOp",EDGE,"E24.filletArc");Q5=makeQuery(id+"F0.imprint","IMPRINT",FACE,{"disambiguationData":[TD([[makeQuery(id+"F0.imprint","IMPRINT",EDGE,{"derivedFrom":subQ11}),1.0]])]});}
            var Q6;
            {var subQ0=sQuery(id+"F0.wireOp",EDGE,"E19.filletArc");var subQ1=sQuery(id+"F0.wireOp",EDGE,"E15.top");var subQ2=makeQuery(id+"F0.imprint","INTERSECT",VERTEX,{"derivedFrom":[subQ1,subQ0]});Q6=makeQuery(id+"F0.imprint","IMPRINT",FACE,{"disambiguationData":[TD([[makeQuery(id+"F0.imprint","IMPRINT",EDGE,{"disambiguationData":[TD([[subQ2,-1.0]])],"derivedFrom":subQ1}),1.0]])]});}
            var Q7;
            {var subQ0=sQuery(id+"F0.wireOp",EDGE,"E18.filletArc");var subQ1=sQuery(id+"F0.wireOp",EDGE,"E15.top");var subQ2=makeQuery(id+"F0.imprint","INTERSECT",VERTEX,{"derivedFrom":[subQ1,subQ0]});Q7=makeQuery(id+"F0.imprint","IMPRINT",FACE,{"disambiguationData":[TD([[makeQuery(id+"F0.imprint","IMPRINT",EDGE,{"disambiguationData":[TD([[subQ2,1.0]])],"derivedFrom":subQ1}),-1.0]])]});}
            var Q8;
            {var subQ0=sQuery(id+"F0.wireOp",EDGE,"E18.filletArc");var subQ1=sQuery(id+"F0.wireOp",EDGE,"E15.top");var subQ2=makeQuery(id+"F0.imprint","INTERSECT",VERTEX,{"derivedFrom":[subQ1,subQ0]});Q8=makeQuery(id+"F0.imprint","IMPRINT",FACE,{"disambiguationData":[TD([[makeQuery(id+"F0.imprint","IMPRINT",EDGE,{"disambiguationData":[TD([[subQ2,1.0]])],"derivedFrom":subQ1}),1.0]])]});}
            var Q9;
            {var subQ0=sQuery(id+"F0.wireOp",EDGE,"E28");var subQ1=sQuery(id+"F0.wireOp",EDGE,"E15.right");var subQ2=makeQuery(id+"F0.imprint","INTERSECT",VERTEX,{"derivedFrom":[subQ1,subQ0]});Q9=makeQuery(id+"F0.imprint","IMPRINT",FACE,{"disambiguationData":[TD([[makeQuery(id+"F0.imprint","IMPRINT",EDGE,{"disambiguationData":[TD([[subQ2,-1.0]])],"derivedFrom":subQ1}),1.0]])]});}
            var Q10;
            {var subQ0=sQuery(id+"F0.wireOp",EDGE,"E17.filletArc");var subQ7=sQuery(id+"F0.wireOp",EDGE,"E15.bottom");var subQ8=makeQuery(id+"F0.imprint","INTERSECT",VERTEX,{"derivedFrom":[subQ7,subQ0]});Q10=makeQuery(id+"F0.imprint","IMPRINT",FACE,{"disambiguationData":[TD([[makeQuery(id+"F0.imprint","IMPRINT",EDGE,{"disambiguationData":[TD([[subQ8,1.0]])],"derivedFrom":subQ7}),-1.0]])]});}
            var Q11;
            {var subQ10=sQuery(id+"F0.wireOp",EDGE,"E22.filletArc");Q11=makeQuery(id+"F0.imprint","IMPRINT",FACE,{"disambiguationData":[TD([[makeQuery(id+"F0.imprint","IMPRINT",EDGE,{"derivedFrom":subQ10}),1.0]])]});}
            var Q12;
            {var subQ1=sQuery(id+"F0.wireOp",EDGE,"E15.top");var subQ7=sQuery(id+"F0.wireOp",EDGE,"E32");var subQ9=makeQuery(id+"F0.imprint","INTERSECT",VERTEX,{"derivedFrom":[subQ1,subQ7]});Q12=makeQuery(id+"F0.imprint","IMPRINT",FACE,{"disambiguationData":[TD([[makeQuery(id+"F0.imprint","IMPRINT",EDGE,{"disambiguationData":[TD([[subQ9,-1.0]])],"derivedFrom":subQ1}),-1.0]])]});}
            var Q13;
            {var subQ0=sQuery(id+"F0.wireOp",EDGE,"E22.filletArc");Q13=makeQuery(id+"F0.imprint","IMPRINT",FACE,{"disambiguationData":[TD([[makeQuery(id+"F0.imprint","IMPRINT",EDGE,{"derivedFrom":subQ0}),-1.0]])]});}
            var Q14;
            {var subQ0=sQuery(id+"F0.wireOp",EDGE,"E21.filletArc");Q14=makeQuery(id+"F0.imprint","IMPRINT",FACE,{"disambiguationData":[TD([[makeQuery(id+"F0.imprint","IMPRINT",EDGE,{"derivedFrom":subQ0}),-1.0]])]});}
            var Q15;
            {var subQ0=sQuery(id+"F0.wireOp",EDGE,"E24.filletArc");Q15=makeQuery(id+"F0.imprint","IMPRINT",FACE,{"disambiguationData":[TD([[makeQuery(id+"F0.imprint","IMPRINT",EDGE,{"derivedFrom":subQ0}),-1.0]])]});}
            var Q16;
            {var subQ0=sQuery(id+"F0.wireOp",EDGE,"E30");var subQ1=sQuery(id+"F0.wireOp",EDGE,"E23.filletArc");var subQ2=makeQuery(id+"F0.imprint","INTERSECT",VERTEX,{"disambiguationData":[OD(0.0)],"derivedFrom":[subQ1,subQ0]});Q16=makeQuery(id+"F0.imprint","IMPRINT",FACE,{"disambiguationData":[TD([[makeQuery(id+"F0.imprint","IMPRINT",EDGE,{"disambiguationData":[TD([[subQ2,-1.0]])],"derivedFrom":subQ1}),-1.0]])]});}
            extrude(context, id + "F5", {"entities" : qUnion([Q0, Q1, Q2, Q3, Q4, Q5, Q6, Q7, Q8, Q9, Q10, Q11, Q12, Q13, Q14, Q15, Q16]), "operationType" : NewBodyOperationType.ADD, "depth" : 20 * mm});
        }
        {
            var Q0;
            Q0=makeQuery(id+"F5.opExtrude","CAP_EDGE",EDGE,{"disambiguationData":[OSD([sQuery(id+"F0.wireOp",EDGE,"E0.left")])],"isStart":true});
            var Q1;
            Q1=makeQuery(id+"F5.opExtrude","CAP_EDGE",EDGE,{"disambiguationData":[OSD([sQuery(id+"F0.wireOp",EDGE,"E3.filletArc")])],"isStart":true});
            var Q2;
            Q2=makeQuery(id+"F5.opExtrude","CAP_EDGE",EDGE,{"disambiguationData":[OSD([sQuery(id+"F0.wireOp",EDGE,"E0.top")])],"isStart":true});
            var Q3;
            Q3=makeQuery(id+"F5.opExtrude","CAP_EDGE",EDGE,{"disambiguationData":[OSD([sQuery(id+"F0.wireOp",EDGE,"E4.filletArc")])],"isStart":true});
            var Q4;
            Q4=makeQuery(id+"F5.opExtrude","CAP_EDGE",EDGE,{"disambiguationData":[OSD([sQuery(id+"F0.wireOp",EDGE,"E0.right")])],"isStart":true});
            var Q5;
            Q5=makeQuery(id+"F5.opExtrude","CAP_EDGE",EDGE,{"disambiguationData":[OSD([sQuery(id+"F0.wireOp",EDGE,"E1.filletArc")])],"isStart":true});
            var Q6;
            Q6=makeQuery(id+"F5.opExtrude","CAP_EDGE",EDGE,{"disambiguationData":[OSD([sQuery(id+"F0.wireOp",EDGE,"E0.bottom")])],"isStart":true});
            var Q7;
            Q7=makeQuery(id+"F5.opExtrude","CAP_EDGE",EDGE,{"disambiguationData":[OSD([sQuery(id+"F0.wireOp",EDGE,"E2.filletArc")])],"isStart":true});
            fillet(context, id + "F6", {"entities" : qUnion([Q0, Q1, Q2, Q3, Q4, Q5, Q6, Q7]), "radius" : 5 * mm, "tangentPropagation" : true, "rho" : 0.5, "crossSection" : FilletCrossSection.CONIC, "allowEdgeOverflow" : false});
        }
    });
